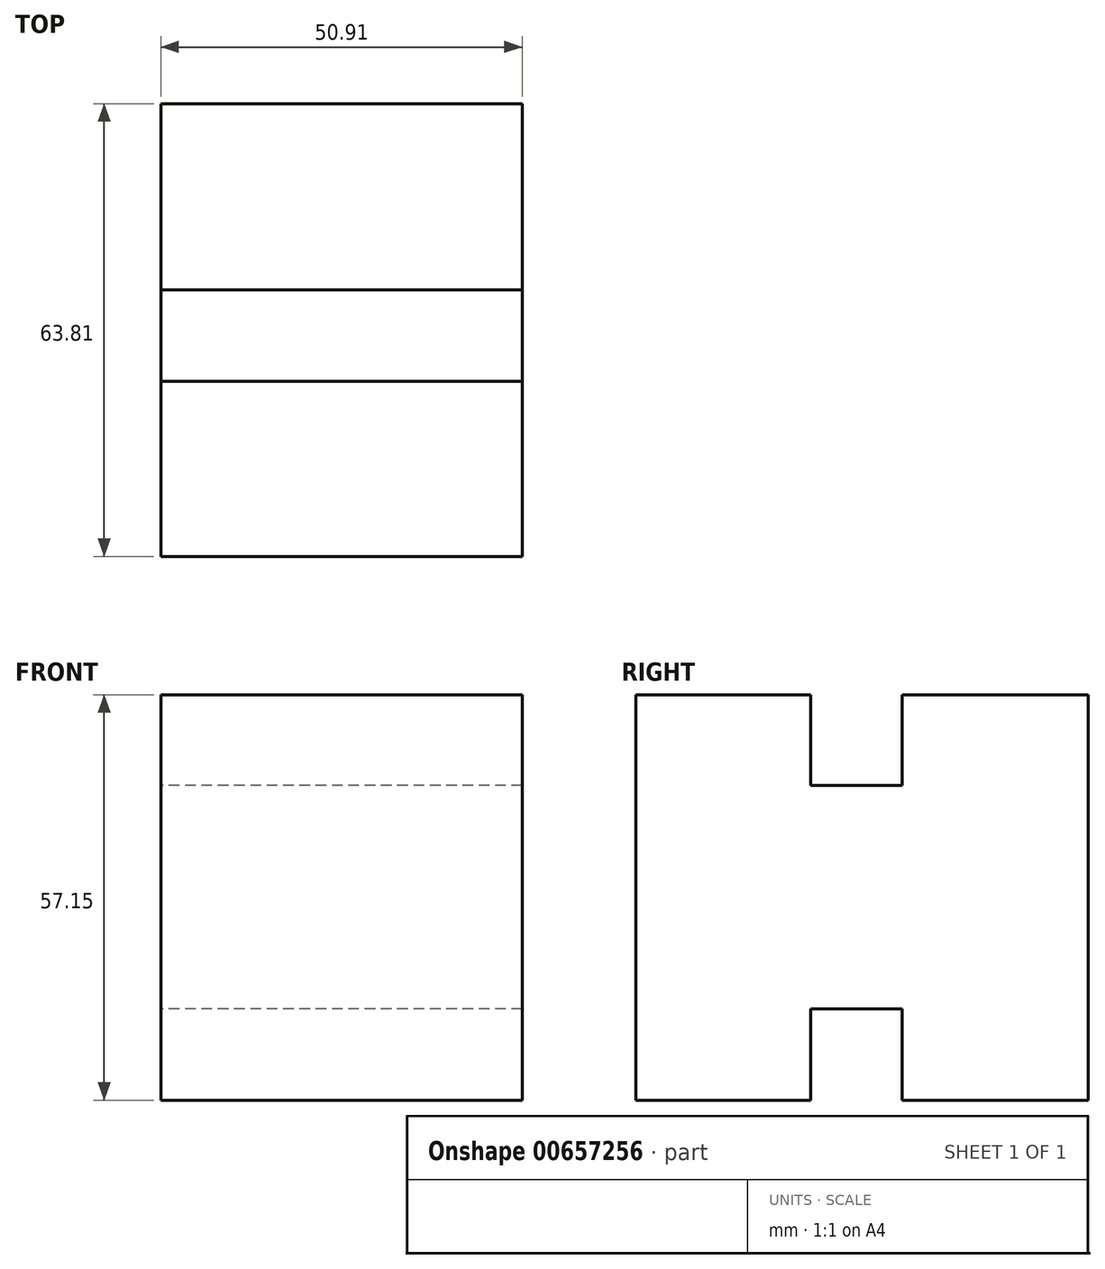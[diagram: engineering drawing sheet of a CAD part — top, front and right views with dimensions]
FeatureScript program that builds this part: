
annotation { "Feature Type Name" : "Feature", "Feature Type Description" : "" }
export const myFeature = defineFeature(function(context is Context, id is Id, definition is map)
    precondition{}
    {
        {
            var Q0;
            Q0=qCreatedBy(makeId("Top.planeOp"),FACE);
            var sketch = newSketch(context, id + "F0", { "sketchPlane" : qUnion([Q0])});
            skLineSegment(sketch, "E0.bottom", {"start": v(-87.46, -8.2) * mm, "end": v(-36.55, -8.2) * mm});
            skLineSegment(sketch, "E0.top", {"start": v(-87.46, 55.6) * mm, "end": v(-36.55, 55.6) * mm});
            skLineSegment(sketch, "E0.left", {"start": v(-87.46, -8.2) * mm, "end": v(-87.46, 55.6) * mm});
            skLineSegment(sketch, "E0.right", {"start": v(-36.55, -8.2) * mm, "end": v(-36.55, 55.6) * mm});
            skSolve(sketch);
        }
        {
            var Q0;
            Q0 = qSketchRegion(id + "F0", true);
            extrude(context, id + "F1", {"entities" : qUnion([Q0]), "depth" : 57.15 * mm, "offsetDistance" : 25.4 * mm});
        }
        {
            var Q0;
            Q0=makeQuery(id+"F1.opExtrude","SWEPT_FACE",FACE,{"disambiguationData":[OSD([sQuery(id+"F0.wireOp",EDGE,"E0.left")])]});
            var sketch = newSketch(context, id + "F2", { "sketchPlane" : qUnion([Q0])});
            skLineSegment(sketch, "E1.bottom", {"start": v(-29.32, 57.15) * mm, "end": v(-16.46, 57.15) * mm});
            skLineSegment(sketch, "E1.top", {"start": v(-29.32, 44.39) * mm, "end": v(-16.46, 44.39) * mm});
            skLineSegment(sketch, "E1.left", {"start": v(-29.32, 57.15) * mm, "end": v(-29.32, 44.39) * mm});
            skLineSegment(sketch, "E1.right", {"start": v(-16.46, 57.15) * mm, "end": v(-16.46, 44.39) * mm});
            skSolve(sketch);
        }
        {
            var Q0;
            Q0=makeQuery(id+"F2.imprint","IMPRINT",FACE,{"disambiguationData":[TD([[makeQuery(id+"F2.imprint","IMPRINT",EDGE,{"derivedFrom":sQuery(id+"F2.wireOp",EDGE,"E1.bottom")}),1.0]])]});
            extrude(context, id + "F3", {"entities" : qUnion([Q0]), "operationType" : NewBodyOperationType.REMOVE, "oppositeDirection" : true, "depth" : 76.2 * mm, "offsetDistance" : 25.4 * mm});
        }
        {
            var Q0;
            Q0=makeQuery(id+"F1.opExtrude","SWEPT_FACE",FACE,{"disambiguationData":[OSD([sQuery(id+"F0.wireOp",EDGE,"E0.left")])]});
            var sketch = newSketch(context, id + "F4", { "sketchPlane" : qUnion([Q0])});
            skLineSegment(sketch, "E2.bottom", {"start": v(-29.32, 0) * mm, "end": v(-16.42, 0) * mm});
            skLineSegment(sketch, "E2.top", {"start": v(-29.32, 12.87) * mm, "end": v(-16.42, 12.87) * mm});
            skLineSegment(sketch, "E2.left", {"start": v(-29.32, 0) * mm, "end": v(-29.32, 12.87) * mm});
            skLineSegment(sketch, "E2.right", {"start": v(-16.42, 0) * mm, "end": v(-16.42, 12.87) * mm});
            skSolve(sketch);
        }
        {
            var Q0;
            Q0 = qSketchRegion(id + "F4", true);
            extrude(context, id + "F5", {"entities" : qUnion([Q0]), "operationType" : NewBodyOperationType.REMOVE, "oppositeDirection" : true, "depth" : 76.2 * mm, "offsetDistance" : 25.4 * mm});
        }
    });
